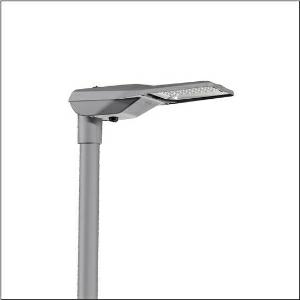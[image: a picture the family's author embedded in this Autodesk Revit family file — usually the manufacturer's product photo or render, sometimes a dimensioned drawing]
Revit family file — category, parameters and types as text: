
# Revit family: streetlight_sl_21_mini___st1_5a_5xe2p33t08gb_e3d2
name_source: partatom
category: Lighting Fixtures
units: mm (PartAtom-declared; Revit-internal decimal feet)

## family parameters
Cut with Voids When Loaded = No
Host = Face
Light Source = No
Part Type = Normal
Room Calculation Point = No
Round Connector Dimension = Use Diameter
Shared = No

## types (1)
- --- (1 x LED, 5840 lm, 40.4 W, 3000K)
    Apparent Load = 40 VA
    CIE Flux Codes = 22 53 95 100 100
    Color Rendering = 70
    Color Temperature = 3000K
    Default Elevation = 1800 mm
    Description = Streetlight SL 21 mini, mast luminaire, primary light control with lens, of PMMA, primary optical cover: cover, of toughened safety glass, transparent, light distribution: ST1.5a, light emission: direct distribution, primary light characteristic: asymmetric, installation type: side-entry, post-top, LED, High Power LED, rated luminous flux: 5.840lm, luminous efficacy: 145lm/W, light colour: 730, colour temperature: 3000K, control gear: D4i, control: overheat protection, constant luminous flux control, time-dependent luminous flux control, flexible luminous flux parameterisation, pre-setting: logarithmic dimming characteristic, mains connection: 220..240V, AC, 50/60Hz, start of lifetime: 40W, end of service life: 41W, reduction: 19W, luminaire housing, of diecast aluminium, powder-coated, Siteco® metallic grey (DB 702S), corrosivity category C5 mid according to DIN EN ISO 12944, please order mast flange separately, inclination adjustable: 0°, 5°, 10°, 15°, sealing non-destructively replaceable, multi-level sealing system, length: 628mm, width: 235mm, height: 110mm, mast flange for spigot size: 42mm (side-entry): 5XC10008XM4, 60/48mm (side-entry/post-top): 5XC10108XM2, 76/60mm (side-entry/post-top): 5XC10108XM1, mounting height: 4..8m, Smart Interface below and above, protection rating (complete): IP66, insulation class (complete): insulation class II (safety insulation), certification: CE, ENEC, ENEC+, VDE, impact resistance: IK10, permissible operating ambient temperature for outdoor applications: -40..+50°C, standard-compliant lighting for roads and squares, packaging unit: 1 piece

Light Distribution: ST1.5a
    Height = 110 mm
    Lamp = 1 x LED
    Lamp Light Flux = 5840 lm
    Lamp Power = 40.4 W
    Lamp count = 1
    Length = 625 mm
    Luminous efficacy = 145 lm/W
    Manufacturer = Siteco
    ModVariant = No
    Model = 5XE2P33T08GB
    Number of Poles = 1
    OnlyDefault = Yes
    Power Factor = 1
    Product Name = Streetlight SL 21 mini | ST1.5a
    Product group = mast luminaire | pylon top
    ProductGroupID = 6100
    Protection Class = Protection class II
    Protection Degree = IP 66
    RLX_Detail_Level = 1
    RLX_Emergency_Light_Flux = 0 lm
    RLX_Emergency_Type = 0
    RLX_Emergency_Type_DB = No
    RlxData = <blob elided: 29885 chars, md5=4d1265bc>
    Socket = socket
    Standby Power = 0 W
    System Light Flux = 5840 lm
    System Power = 40 W
    Type Comments = factory setting: luminous flux: 100 % | dim-lin: 254 | 812 mA
    Type Image = l_1003514.jpg
    URL = http://relux.com
    VarID = @adj_197039
    Voltage = 0 V
    Weight = 0.00 kg
    Width = 234 mm

## geometry (parser evidence)
native form markers: Blend x4, Sweep x8
no freeform markers — native parametric forms only
